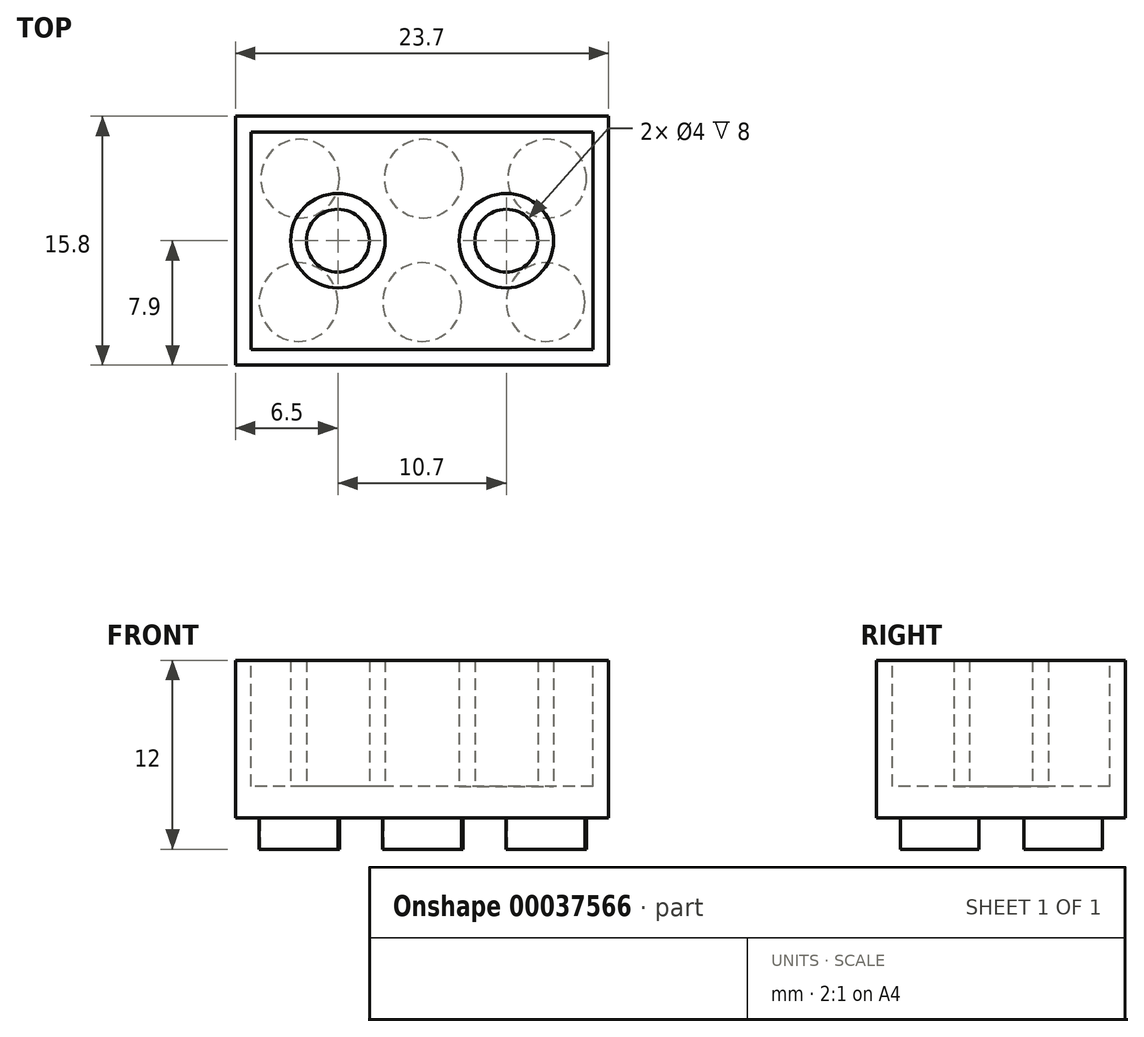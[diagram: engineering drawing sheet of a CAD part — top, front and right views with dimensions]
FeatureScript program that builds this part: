
annotation { "Feature Type Name" : "Feature", "Feature Type Description" : "" }
export const myFeature = defineFeature(function(context is Context, id is Id, definition is map)
    precondition{}
    {
        {
            var Q0;
            Q0=qCreatedBy(makeId("Top.planeOp"),FACE);
            var sketch = newSketch(context, id + "F0", { "sketchPlane" : qUnion([Q0])});
            skLineSegment(sketch, "E0.rect.bottom", {"start": v(11.85, 7.9) * mm, "end": v(-11.85, 7.9) * mm});
            skLineSegment(sketch, "E0.rect.top", {"start": v(11.85, -7.9) * mm, "end": v(-11.85, -7.9) * mm});
            skLineSegment(sketch, "E0.rect.left", {"start": v(11.85, 7.9) * mm, "end": v(11.85, -7.9) * mm});
            skLineSegment(sketch, "E0.rect.right", {"start": v(-11.85, 7.9) * mm, "end": v(-11.85, -7.9) * mm});
            skPoint(sketch, "E0.rect.middle", {"position": v(0, 0) * mm});
            skSolve(sketch);
        }
        {
            var Q0;
            Q0=makeQuery(id+"F0.imprint","IMPRINT",FACE,{"disambiguationData":[TD([[makeQuery(id+"F0.imprint","IMPRINT",EDGE,{"derivedFrom":sQuery(id+"F0.wireOp",EDGE,"E0.rect.bottom")}),1.0]])]});
            extrude(context, id + "F1", {"entities" : qUnion([Q0]), "depth" : 10 * mm});
        }
        {
            var Q0;
            Q0=qCreatedBy(makeId("Top.planeOp"),FACE);
            var sketch = newSketch(context, id + "F2", { "sketchPlane" : qUnion([Q0])});
            skCircle(sketch, "E1", {"center": v(-6.85, 3.5) * mm, "radius": 2.5 * mm});
            skSolve(sketch);
        }
        {
            var Q0;
            Q0=qCreatedBy(makeId("Top.planeOp"),FACE);
            var sketch = newSketch(context, id + "F3", { "sketchPlane" : qUnion([Q0])});
            skCircle(sketch, "E2", {"center": v(0, 3.4) * mm, "radius": 2.5 * mm});
            skSolve(sketch);
        }
        {
            var Q0;
            Q0=qCreatedBy(makeId("Top.planeOp"),FACE);
            var sketch = newSketch(context, id + "F4", { "sketchPlane" : qUnion([Q0])});
            skCircle(sketch, "E3", {"center": v(7.35, 3.4) * mm, "radius": 2.5 * mm});
            skSolve(sketch);
        }
        {
            var Q0;
            Q0=qCreatedBy(makeId("Top.planeOp"),FACE);
            var sketch = newSketch(context, id + "F5", { "sketchPlane" : qUnion([Q0])});
            skCircle(sketch, "E4", {"center": v(0, -3.4) * mm, "radius": 2.5 * mm});
            skSolve(sketch);
        }
        {
            var Q0;
            Q0=qCreatedBy(makeId("Top.planeOp"),FACE);
            var sketch = newSketch(context, id + "F6", { "sketchPlane" : qUnion([Q0])});
            skCircle(sketch, "E5", {"center": v(7.35, -3.4) * mm, "radius": 2.5 * mm});
            skSolve(sketch);
        }
        {
            var Q0;
            Q0=qCreatedBy(makeId("Top.planeOp"),FACE);
            var sketch = newSketch(context, id + "F7", { "sketchPlane" : qUnion([Q0])});
            skCircle(sketch, "E6", {"center": v(-6.85, -3.4) * mm, "radius": 2.5 * mm});
            skSolve(sketch);
        }
        {
            var Q0;
            Q0=sQuery(id+"F2.wireOp",EDGE,"E1");
            var Q1;
            Q1=sQuery(id+"F3.wireOp",EDGE,"E2");
            var Q2;
            Q2=sQuery(id+"F4.wireOp",EDGE,"E3");
            var Q3;
            Q3=sQuery(id+"F6.wireOp",EDGE,"E5");
            var Q4;
            Q4=sQuery(id+"F5.wireOp",EDGE,"E4");
            var Q5;
            Q5=sQuery(id+"F7.wireOp",EDGE,"E6");
            extrude(context, id + "F8", {"bodyType" : ToolBodyType.SURFACE, "surfaceEntities" : qUnion([Q0, Q1, Q2, Q3, Q4, Q5]), "oppositeDirection" : true, "depth" : 5 * mm});
        }
        {
            var Q0;
            Q0=makeQuery(id+"F1.opExtrude","CAP_FACE",FACE,{"disambiguationData":[OSD([sQuery(id+"F0.wireOp",EDGE,"E0.rect.bottom"),sQuery(id+"F0.wireOp",EDGE,"E0.rect.top"),sQuery(id+"F0.wireOp",EDGE,"E0.rect.left"),sQuery(id+"F0.wireOp",EDGE,"E0.rect.right")])],"isStart":false});
            var sketch = newSketch(context, id + "F9", { "sketchPlane" : qUnion([Q0])});
            skLineSegment(sketch, "E7.rect.bottom", {"start": v(10.85, 6.9) * mm, "end": v(-10.85, 6.9) * mm});
            skLineSegment(sketch, "E7.rect.top", {"start": v(10.85, -6.9) * mm, "end": v(-10.85, -6.9) * mm});
            skLineSegment(sketch, "E7.rect.left", {"start": v(10.85, 6.9) * mm, "end": v(10.85, -6.9) * mm});
            skLineSegment(sketch, "E7.rect.right", {"start": v(-10.85, 6.9) * mm, "end": v(-10.85, -6.9) * mm});
            skPoint(sketch, "E7.rect.middle", {"position": v(0, 0) * mm});
            skSolve(sketch);
        }
        {
            var Q0;
            Q0 = qSketchRegion(id + "F9", true);
            extrude(context, id + "F10", {"entities" : qUnion([Q0]), "operationType" : NewBodyOperationType.REMOVE, "oppositeDirection" : true, "depth" : 8 * mm});
        }
        {
            var Q0;
            Q0=makeQuery(id+"F10.boolean.opBoolean","COPY",FACE,{"derivedFrom":makeQuery(id+"F10.opExtrude","CAP_FACE",FACE,{"disambiguationData":[OSD([sQuery(id+"F9.wireOp",EDGE,"E7.rect.bottom"),sQuery(id+"F9.wireOp",EDGE,"E7.rect.top"),sQuery(id+"F9.wireOp",EDGE,"E7.rect.left"),sQuery(id+"F9.wireOp",EDGE,"E7.rect.right")])],"isStart":false})});
            var sketch = newSketch(context, id + "F11", { "sketchPlane" : qUnion([Q0])});
            skCircle(sketch, "E8", {"center": v(-5.35, 0) * mm, "radius": 3 * mm});
            skCircle(sketch, "E9", {"center": v(-5.35, 0) * mm, "radius": 2 * mm});
            skSolve(sketch);
        }
        {
            var Q0;
            Q0 = qSketchRegion(id + "F11", true);
            var Q1;
            Q1=makeQuery(id+"F1.opExtrude","CAP_FACE",FACE,{"disambiguationData":[OSD([sQuery(id+"F0.wireOp",EDGE,"E0.rect.bottom"),sQuery(id+"F0.wireOp",EDGE,"E0.rect.top"),sQuery(id+"F0.wireOp",EDGE,"E0.rect.left"),sQuery(id+"F0.wireOp",EDGE,"E0.rect.right")])],"isStart":false});
            extrude(context, id + "F12", {"entities" : qUnion([Q0]), "endBound" : BoundingType.UP_TO_SURFACE, "endBoundEntityFace" : qUnion([Q1]), "depth" : 8 * mm});
        }
        {
            var Q0;
            Q0=makeQuery(id+"F12.opExtrude","SWEPT_BODY",BODY,{"disambiguationData":[OSD([sQuery(id+"F11.wireOp",EDGE,"E8"),sQuery(id+"F11.wireOp",EDGE,"E9")])]});
            var Q1;
            Q1=qCreatedBy(makeId("Right.planeOp"),FACE);
            mirror(context, id + "F13", {"operationType" : NewBodyOperationType.ADD, "entities" : qUnion([Q0]), "mirrorPlane" : qUnion([Q1])});
        }
        {
            var Q0;
            Q0=makeQuery(id+"F8.opExtrude","SWEPT_BODY",BODY,{"disambiguationData":[OSD([sQuery(id+"F2.wireOp",EDGE,"E1")])]});
            var Q1;
            Q1=makeQuery(id+"F8.opExtrude","SWEPT_BODY",BODY,{"disambiguationData":[OSD([sQuery(id+"F3.wireOp",EDGE,"E2")])]});
            var Q2;
            Q2=makeQuery(id+"F8.opExtrude","SWEPT_BODY",BODY,{"disambiguationData":[OSD([sQuery(id+"F4.wireOp",EDGE,"E3")])]});
            var Q3;
            Q3=makeQuery(id+"F8.opExtrude","SWEPT_BODY",BODY,{"disambiguationData":[OSD([sQuery(id+"F6.wireOp",EDGE,"E5")])]});
            var Q4;
            Q4=makeQuery(id+"F8.opExtrude","SWEPT_BODY",BODY,{"disambiguationData":[OSD([sQuery(id+"F5.wireOp",EDGE,"E4")])]});
            var Q5;
            Q5=makeQuery(id+"F8.opExtrude","SWEPT_BODY",BODY,{"disambiguationData":[OSD([sQuery(id+"F7.wireOp",EDGE,"E6")])]});
            deleteBodies(context, id + "F14", {"entities" : qUnion([Q0, Q1, Q2, Q3, Q4, Q5])});
        }
        {
            var Q0;
            Q0=makeQuery(id+"F1.opExtrude","CAP_FACE",FACE,{"disambiguationData":[OSD([sQuery(id+"F0.wireOp",EDGE,"E0.rect.bottom"),sQuery(id+"F0.wireOp",EDGE,"E0.rect.top"),sQuery(id+"F0.wireOp",EDGE,"E0.rect.left"),sQuery(id+"F0.wireOp",EDGE,"E0.rect.right")])],"isStart":true});
            var sketch = newSketch(context, id + "F15", { "sketchPlane" : qUnion([Q0])});
            skCircle(sketch, "E10", {"center": v(-7.85, 3.9) * mm, "radius": 2.5 * mm});
            skCircle(sketch, "E11.1.0.0", {"center": v(0, 3.9) * mm, "radius": 2.5 * mm});
            skCircle(sketch, "E11.2.0.0", {"center": v(7.85, 3.9) * mm, "radius": 2.5 * mm});
            skLineSegment(sketch, "E11.direction1", {"start": v(-7.85, 3.9) * mm, "end": v(0, 3.9) * mm, "construction": true});
            skCircle(sketch, "E12.1.0.0", {"center": v(7.94, -3.94) * mm, "radius": 2.5 * mm});
            skCircle(sketch, "E12.1.0.1", {"center": v(0.1, -3.94) * mm, "radius": 2.5 * mm});
            skCircle(sketch, "E12.1.0.2", {"center": v(-7.75, -3.94) * mm, "radius": 2.5 * mm});
            skLineSegment(sketch, "E12.direction1", {"start": v(7.85, 3.9) * mm, "end": v(7.94, -3.94) * mm, "construction": true});
            skSolve(sketch);
        }
        {
            var Q0;
            Q0=makeQuery(id+"F15.imprint","IMPRINT",FACE,{"disambiguationData":[TD([[makeQuery(id+"F15.imprint","IMPRINT",EDGE,{"derivedFrom":sQuery(id+"F15.wireOp",EDGE,"E12.1.0.2")}),1.0]])]});
            var Q1;
            Q1=makeQuery(id+"F15.imprint","IMPRINT",FACE,{"disambiguationData":[TD([[makeQuery(id+"F15.imprint","IMPRINT",EDGE,{"derivedFrom":sQuery(id+"F15.wireOp",EDGE,"E10")}),1.0]])]});
            var Q2;
            Q2=makeQuery(id+"F15.imprint","IMPRINT",FACE,{"disambiguationData":[TD([[makeQuery(id+"F15.imprint","IMPRINT",EDGE,{"derivedFrom":sQuery(id+"F15.wireOp",EDGE,"E11.1.0.0")}),1.0]])]});
            var Q3;
            Q3=makeQuery(id+"F15.imprint","IMPRINT",FACE,{"disambiguationData":[TD([[makeQuery(id+"F15.imprint","IMPRINT",EDGE,{"derivedFrom":sQuery(id+"F15.wireOp",EDGE,"E11.2.0.0")}),1.0]])]});
            var Q4;
            Q4=makeQuery(id+"F15.imprint","IMPRINT",FACE,{"disambiguationData":[TD([[makeQuery(id+"F15.imprint","IMPRINT",EDGE,{"derivedFrom":sQuery(id+"F15.wireOp",EDGE,"E12.1.0.0")}),1.0]])]});
            var Q5;
            Q5=makeQuery(id+"F15.imprint","IMPRINT",FACE,{"disambiguationData":[TD([[makeQuery(id+"F15.imprint","IMPRINT",EDGE,{"derivedFrom":sQuery(id+"F15.wireOp",EDGE,"E12.1.0.1")}),1.0]])]});
            extrude(context, id + "F16", {"entities" : qUnion([Q0, Q1, Q2, Q3, Q4, Q5]), "depth" : 2 * mm});
        }
    });
